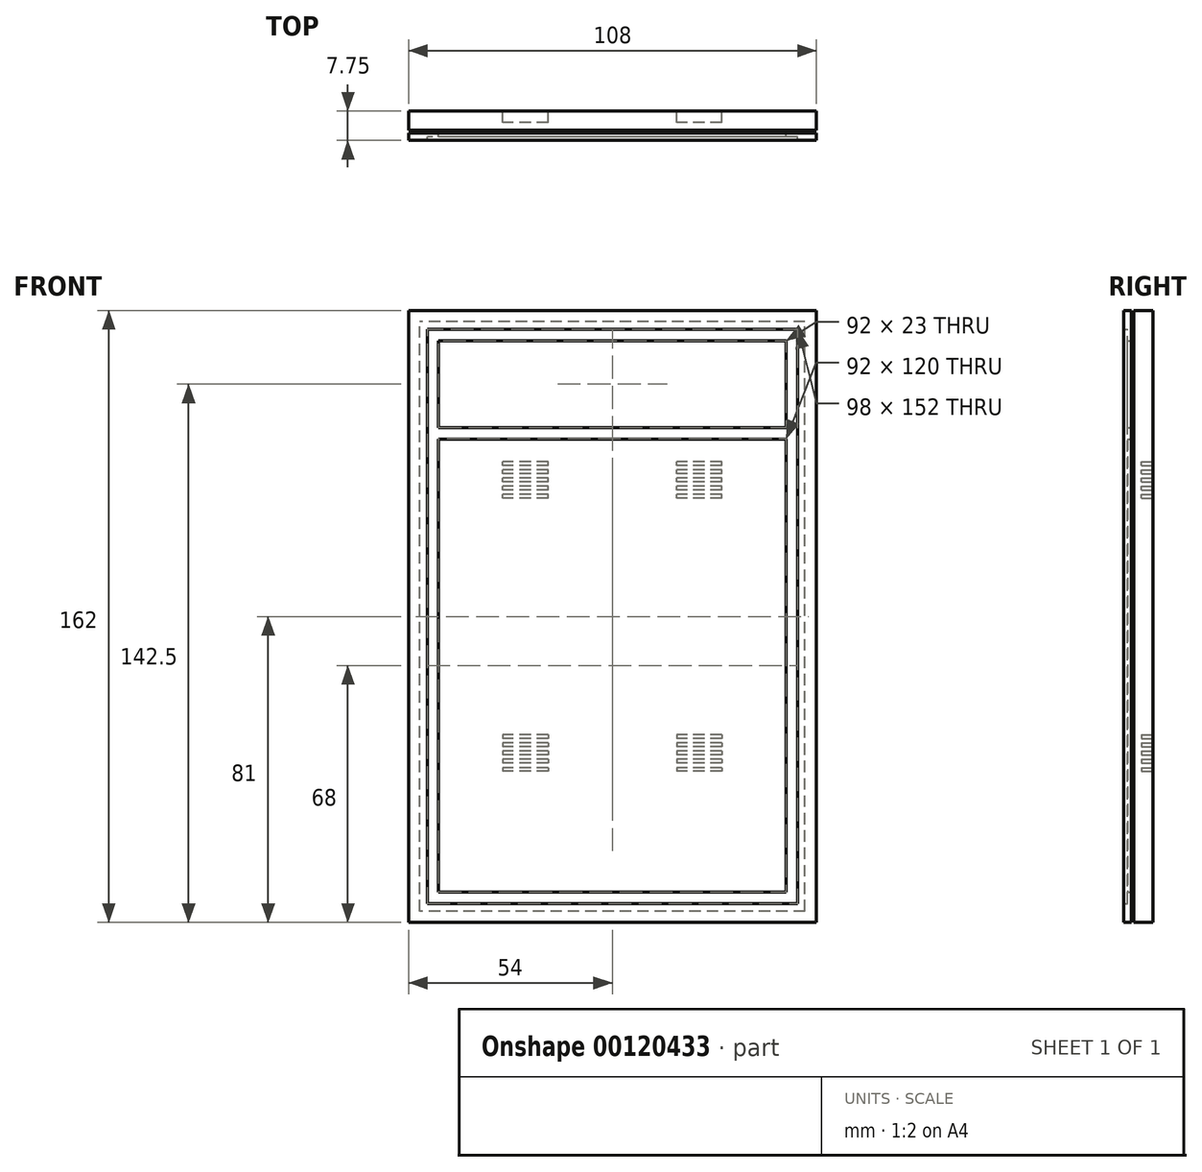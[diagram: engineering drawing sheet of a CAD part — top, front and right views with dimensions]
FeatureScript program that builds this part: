
annotation { "Feature Type Name" : "Feature", "Feature Type Description" : "" }
export const myFeature = defineFeature(function(context is Context, id is Id, definition is map)
    precondition{}
    {
        {
            var Q0;
            Q0=qCreatedBy(makeId("Front.planeOp"),FACE);
            var sketch = newSketch(context, id + "F0", { "sketchPlane" : qUnion([Q0])});
            skLineSegment(sketch, "E0.bottom", {"start": v(54, -81) * mm, "end": v(-54, -81) * mm});
            skLineSegment(sketch, "E0.top", {"start": v(54, 81) * mm, "end": v(-54, 81) * mm});
            skLineSegment(sketch, "E0.left", {"start": v(54, -81) * mm, "end": v(54, 81) * mm});
            skLineSegment(sketch, "E0.right", {"start": v(-54, -81) * mm, "end": v(-54, 81) * mm});
            skPoint(sketch, "E0.middle", {"position": v(0, 0) * mm});
            skLineSegment(sketch, "E1.0", {"start": v(49, 76) * mm, "end": v(-49, 76) * mm});
            skLineSegment(sketch, "E1.1", {"start": v(49, -76) * mm, "end": v(49, 76) * mm});
            skLineSegment(sketch, "E1.2", {"start": v(49, -76) * mm, "end": v(-49, -76) * mm});
            skLineSegment(sketch, "E1.3", {"start": v(-49, -76) * mm, "end": v(-49, 76) * mm});
            skLineSegment(sketch, "E2.bottom", {"start": v(46, -73) * mm, "end": v(-46, -73) * mm});
            skLineSegment(sketch, "E2.top", {"start": v(46, 50) * mm, "end": v(-46, 50) * mm});
            skLineSegment(sketch, "E2.right", {"start": v(-46, -73) * mm, "end": v(-46, 47) * mm});
            skPoint(sketch, "E2.middle", {"position": v(0, -11.5) * mm});
            skLineSegment(sketch, "E3.top", {"start": v(-46, 73) * mm, "end": v(46, 73) * mm});
            skLineSegment(sketch, "E3.left", {"start": v(-46, 50) * mm, "end": v(-46, 73) * mm});
            skLineSegment(sketch, "E3.right", {"start": v(46, 50) * mm, "end": v(46, 73) * mm});
            skLineSegment(sketch, "E4", {"start": v(-46, 47) * mm, "end": v(46, 47) * mm});
            skLineSegment(sketch, "E5", {"start": v(46, 47) * mm, "end": v(46, -73) * mm});
            skLineSegment(sketch, "E6.0", {"start": v(51, 78) * mm, "end": v(-51, 78) * mm});
            skLineSegment(sketch, "E6.1", {"start": v(51, -78) * mm, "end": v(51, 78) * mm});
            skLineSegment(sketch, "E6.2", {"start": v(51, -78) * mm, "end": v(-51, -78) * mm});
            skLineSegment(sketch, "E6.3", {"start": v(-51, -78) * mm, "end": v(-51, 78) * mm});
            skSolve(sketch);
        }
        {
            var Q0;
            Q0=makeQuery(id+"F0.imprint","IMPRINT",FACE,{"disambiguationData":[TD([[makeQuery(id+"F0.imprint","IMPRINT",EDGE,{"derivedFrom":sQuery(id+"F0.wireOp",EDGE,"E0.bottom")}),-1.0]])]});
            var Q1;
            Q1=makeQuery(id+"F0.imprint","IMPRINT",FACE,{"disambiguationData":[TD([[makeQuery(id+"F0.imprint","IMPRINT",EDGE,{"derivedFrom":sQuery(id+"F0.wireOp",EDGE,"E1.0")}),-1.0]])]});
            extrude(context, id + "F1", {"entities" : qUnion([Q0, Q1]), "depth" : 2 * mm});
        }
        {
            var Q0;
            Q0=makeQuery(id+"F0.imprint","IMPRINT",FACE,{"disambiguationData":[TD([[makeQuery(id+"F0.imprint","IMPRINT",EDGE,{"derivedFrom":sQuery(id+"F0.wireOp",EDGE,"E1.0")}),1.0]])]});
            extrude(context, id + "F2", {"entities" : qUnion([Q0]), "depth" : 1 * mm});
        }
        {
            var Q0;
            Q0=makeQuery(id+"F0.imprint","IMPRINT",FACE,{"disambiguationData":[TD([[makeQuery(id+"F0.imprint","IMPRINT",EDGE,{"derivedFrom":sQuery(id+"F0.wireOp",EDGE,"E2.bottom")}),-1.0]])]});
            extrude(context, id + "F3", {"entities" : qUnion([Q0]), "depth" : 1 * mm});
        }
        {
            var Q0;
            Q0=makeQuery(id+"F0.imprint","IMPRINT",FACE,{"disambiguationData":[TD([[makeQuery(id+"F0.imprint","IMPRINT",EDGE,{"derivedFrom":sQuery(id+"F0.wireOp",EDGE,"E2.top")}),-1.0]])]});
            extrude(context, id + "F4", {"entities" : qUnion([Q0]), "depth" : 1 * mm});
        }
        {
            var Q0;
            Q0=makeQuery(id+"F0.imprint","IMPRINT",FACE,{"disambiguationData":[TD([[makeQuery(id+"F0.imprint","IMPRINT",EDGE,{"derivedFrom":sQuery(id+"F0.wireOp",EDGE,"E1.0")}),-1.0]])]});
            extrude(context, id + "F5", {"entities" : qUnion([Q0]), "operationType" : NewBodyOperationType.ADD, "oppositeDirection" : true, "depth" : 0.75 * mm});
        }
        {
            var Q0;
            Q0=makeQuery(id+"F0.imprint","IMPRINT",FACE,{"disambiguationData":[TD([[makeQuery(id+"F0.imprint","IMPRINT",EDGE,{"derivedFrom":sQuery(id+"F0.wireOp",EDGE,"E0.bottom")}),-1.0]])]});
            var Q1;
            Q1=makeQuery(id+"F0.imprint","IMPRINT",FACE,{"disambiguationData":[TD([[makeQuery(id+"F0.imprint","IMPRINT",EDGE,{"derivedFrom":sQuery(id+"F0.wireOp",EDGE,"E1.0")}),-1.0]])]});
            var Q2;
            Q2=makeQuery(id+"F0.imprint","IMPRINT",FACE,{"disambiguationData":[TD([[makeQuery(id+"F0.imprint","IMPRINT",EDGE,{"derivedFrom":sQuery(id+"F0.wireOp",EDGE,"E1.0")}),1.0]])]});
            var Q3;
            Q3=makeQuery(id+"F0.imprint","IMPRINT",FACE,{"disambiguationData":[TD([[makeQuery(id+"F0.imprint","IMPRINT",EDGE,{"derivedFrom":sQuery(id+"F0.wireOp",EDGE,"E2.top")}),-1.0]])]});
            var Q4;
            Q4=makeQuery(id+"F0.imprint","IMPRINT",FACE,{"disambiguationData":[TD([[makeQuery(id+"F0.imprint","IMPRINT",EDGE,{"derivedFrom":sQuery(id+"F0.wireOp",EDGE,"E2.bottom")}),-1.0]])]});
            extrude(context, id + "F6", {"entities" : qUnion([Q0, Q1, Q2, Q3, Q4]), "oppositeDirection" : true, "depth" : 5 * mm});
        }
        {
            var Q0;
            Q0=makeQuery(id+"F6.opExtrude","SWEPT_BODY",BODY,{"disambiguationData":[OSD([sQuery(id+"F0.wireOp",EDGE,"E0.bottom"),sQuery(id+"F0.wireOp",EDGE,"E0.top"),sQuery(id+"F0.wireOp",EDGE,"E0.left"),sQuery(id+"F0.wireOp",EDGE,"E0.right")])]});
            transform(context, id + "F7", {"entities" : qUnion([Q0]), "transformType" : TransformType.TRANSLATION_3D, "dx" : 0 * mm, "dy" : 0.75 * mm, "dz" : 0 * mm, "makeCopy" : false});
        }
        {
            var Q0;
            Q0=makeQuery(id+"F6.opExtrude","CAP_FACE",FACE,{"disambiguationData":[OSD([sQuery(id+"F0.wireOp",EDGE,"E0.bottom"),sQuery(id+"F0.wireOp",EDGE,"E0.top"),sQuery(id+"F0.wireOp",EDGE,"E0.left"),sQuery(id+"F0.wireOp",EDGE,"E0.right")])],"isStart":false});
            var sketch = newSketch(context, id + "F8", { "sketchPlane" : qUnion([Q0])});
            skLineSegment(sketch, "E7.bottom", {"start": v(-29, -40) * mm, "end": v(-17, -40) * mm});
            skLineSegment(sketch, "E7.top", {"start": v(-29, -41) * mm, "end": v(-17, -41) * mm});
            skLineSegment(sketch, "E7.left", {"start": v(-29, -40) * mm, "end": v(-29, -41) * mm});
            skLineSegment(sketch, "E7.right", {"start": v(-17, -40) * mm, "end": v(-17, -41) * mm});
            skLineSegment(sketch, "E8.0.1.0", {"start": v(-29, -37.82) * mm, "end": v(-17, -37.82) * mm});
            skLineSegment(sketch, "E8.0.1.1", {"start": v(-29, -38.82) * mm, "end": v(-17, -38.82) * mm});
            skLineSegment(sketch, "E8.0.1.2", {"start": v(-17, -37.82) * mm, "end": v(-17, -38.82) * mm});
            skLineSegment(sketch, "E8.0.1.3", {"start": v(-29, -37.82) * mm, "end": v(-29, -38.82) * mm});
            skLineSegment(sketch, "E8.0.2.0", {"start": v(-29, -35.64) * mm, "end": v(-17, -35.64) * mm});
            skLineSegment(sketch, "E8.0.2.1", {"start": v(-29, -36.64) * mm, "end": v(-17, -36.64) * mm});
            skLineSegment(sketch, "E8.0.2.2", {"start": v(-17, -35.64) * mm, "end": v(-17, -36.64) * mm});
            skLineSegment(sketch, "E8.0.2.3", {"start": v(-29, -35.64) * mm, "end": v(-29, -36.64) * mm});
            skLineSegment(sketch, "E8.0.3.0", {"start": v(-29, -33.45) * mm, "end": v(-17, -33.45) * mm});
            skLineSegment(sketch, "E8.0.3.1", {"start": v(-29, -34.45) * mm, "end": v(-17, -34.45) * mm});
            skLineSegment(sketch, "E8.0.3.2", {"start": v(-17, -33.45) * mm, "end": v(-17, -34.45) * mm});
            skLineSegment(sketch, "E8.0.3.3", {"start": v(-29, -33.45) * mm, "end": v(-29, -34.45) * mm});
            skLineSegment(sketch, "E8.0.4.0", {"start": v(-29, -31.27) * mm, "end": v(-17, -31.27) * mm});
            skLineSegment(sketch, "E8.0.4.1", {"start": v(-29, -32.27) * mm, "end": v(-17, -32.27) * mm});
            skLineSegment(sketch, "E8.0.4.2", {"start": v(-17, -31.27) * mm, "end": v(-17, -32.27) * mm});
            skLineSegment(sketch, "E8.0.4.3", {"start": v(-29, -31.27) * mm, "end": v(-29, -32.27) * mm});
            skLineSegment(sketch, "E8.1.0.0", {"start": v(17, -40) * mm, "end": v(29, -40) * mm});
            skLineSegment(sketch, "E8.1.0.1", {"start": v(17, -41) * mm, "end": v(29, -41) * mm});
            skLineSegment(sketch, "E8.1.0.2", {"start": v(29, -40) * mm, "end": v(29, -41) * mm});
            skLineSegment(sketch, "E8.1.0.3", {"start": v(17, -40) * mm, "end": v(17, -41) * mm});
            skLineSegment(sketch, "E8.1.1.0", {"start": v(17, -37.82) * mm, "end": v(29, -37.82) * mm});
            skLineSegment(sketch, "E8.1.1.1", {"start": v(17, -38.82) * mm, "end": v(29, -38.82) * mm});
            skLineSegment(sketch, "E8.1.1.2", {"start": v(29, -37.82) * mm, "end": v(29, -38.82) * mm});
            skLineSegment(sketch, "E8.1.1.3", {"start": v(17, -37.82) * mm, "end": v(17, -38.82) * mm});
            skLineSegment(sketch, "E8.1.2.0", {"start": v(17, -35.64) * mm, "end": v(29, -35.64) * mm});
            skLineSegment(sketch, "E8.1.2.1", {"start": v(17, -36.64) * mm, "end": v(29, -36.64) * mm});
            skLineSegment(sketch, "E8.1.2.2", {"start": v(29, -35.64) * mm, "end": v(29, -36.64) * mm});
            skLineSegment(sketch, "E8.1.2.3", {"start": v(17, -35.64) * mm, "end": v(17, -36.64) * mm});
            skLineSegment(sketch, "E8.1.3.0", {"start": v(17, -33.45) * mm, "end": v(29, -33.45) * mm});
            skLineSegment(sketch, "E8.1.3.1", {"start": v(17, -34.45) * mm, "end": v(29, -34.45) * mm});
            skLineSegment(sketch, "E8.1.3.2", {"start": v(29, -33.45) * mm, "end": v(29, -34.45) * mm});
            skLineSegment(sketch, "E8.1.3.3", {"start": v(17, -33.45) * mm, "end": v(17, -34.45) * mm});
            skLineSegment(sketch, "E8.1.4.0", {"start": v(17, -31.27) * mm, "end": v(29, -31.27) * mm});
            skLineSegment(sketch, "E8.1.4.1", {"start": v(17, -32.27) * mm, "end": v(29, -32.27) * mm});
            skLineSegment(sketch, "E8.1.4.2", {"start": v(29, -31.27) * mm, "end": v(29, -32.27) * mm});
            skLineSegment(sketch, "E8.1.4.3", {"start": v(17, -31.27) * mm, "end": v(17, -32.27) * mm});
            skLineSegment(sketch, "E8.direction1", {"start": v(-29, -40) * mm, "end": v(17, -40) * mm, "construction": true});
            skLineSegment(sketch, "E8.direction2", {"start": v(-29, -40) * mm, "end": v(-29, -37.82) * mm, "construction": true});
            skLineSegment(sketch, "E9.MirrorCS", {"start": v(-29, 40) * mm, "end": v(-29, 37.82) * mm, "construction": true});
            skLineSegment(sketch, "E10.MirrorCS", {"start": v(-17, 33.45) * mm, "end": v(-17, 34.45) * mm});
            skLineSegment(sketch, "E11.MirrorCS", {"start": v(-29, 33.45) * mm, "end": v(-29, 34.45) * mm});
            skLineSegment(sketch, "E12.MirrorCS", {"start": v(-29, 40) * mm, "end": v(-29, 41) * mm});
            skLineSegment(sketch, "E13.MirrorCS", {"start": v(-29, 37.82) * mm, "end": v(-29, 38.82) * mm});
            skLineSegment(sketch, "E14.MirrorCS", {"start": v(-17, 40) * mm, "end": v(-17, 41) * mm});
            skLineSegment(sketch, "E15.MirrorCS", {"start": v(-29, 31.27) * mm, "end": v(-29, 32.27) * mm});
            skLineSegment(sketch, "E16.MirrorCS", {"start": v(-29, 35.64) * mm, "end": v(-29, 36.64) * mm});
            skLineSegment(sketch, "E17.MirrorCS", {"start": v(-17, 35.64) * mm, "end": v(-17, 36.64) * mm});
            skLineSegment(sketch, "E18.MirrorCS", {"start": v(-17, 37.82) * mm, "end": v(-17, 38.82) * mm});
            skLineSegment(sketch, "E19.MirrorCS", {"start": v(-17, 31.27) * mm, "end": v(-17, 32.27) * mm});
            skLineSegment(sketch, "E20.MirrorCS", {"start": v(-29, 32.27) * mm, "end": v(-17, 32.27) * mm});
            skLineSegment(sketch, "E21.MirrorCS", {"start": v(-29, 34.45) * mm, "end": v(-17, 34.45) * mm});
            skLineSegment(sketch, "E22.MirrorCS", {"start": v(-29, 40) * mm, "end": v(-17, 40) * mm});
            skLineSegment(sketch, "E23.MirrorCS", {"start": v(-29, 41) * mm, "end": v(-17, 41) * mm});
            skLineSegment(sketch, "E24.MirrorCS", {"start": v(-29, 37.82) * mm, "end": v(-17, 37.82) * mm});
            skLineSegment(sketch, "E25.MirrorCS", {"start": v(-29, 33.45) * mm, "end": v(-17, 33.45) * mm});
            skLineSegment(sketch, "E26.MirrorCS", {"start": v(-29, 36.64) * mm, "end": v(-17, 36.64) * mm});
            skLineSegment(sketch, "E27.MirrorCS", {"start": v(-29, 35.64) * mm, "end": v(-17, 35.64) * mm});
            skLineSegment(sketch, "E28.MirrorCS", {"start": v(-29, 31.27) * mm, "end": v(-17, 31.27) * mm});
            skLineSegment(sketch, "E29.MirrorCS", {"start": v(-29, 38.82) * mm, "end": v(-17, 38.82) * mm});
            skLineSegment(sketch, "E30.MirrorCS", {"start": v(17, 40) * mm, "end": v(17, 41) * mm});
            skLineSegment(sketch, "E31.MirrorCS", {"start": v(17, 35.64) * mm, "end": v(17, 36.64) * mm});
            skLineSegment(sketch, "E32.MirrorCS", {"start": v(29, 33.45) * mm, "end": v(29, 34.45) * mm});
            skLineSegment(sketch, "E33.MirrorCS", {"start": v(17, 37.82) * mm, "end": v(17, 38.82) * mm});
            skLineSegment(sketch, "E34.MirrorCS", {"start": v(29, 40) * mm, "end": v(29, 41) * mm});
            skLineSegment(sketch, "E35.MirrorCS", {"start": v(29, 31.27) * mm, "end": v(29, 32.27) * mm});
            skLineSegment(sketch, "E36.MirrorCS", {"start": v(29, 37.82) * mm, "end": v(29, 38.82) * mm});
            skLineSegment(sketch, "E37.MirrorCS", {"start": v(29, 35.64) * mm, "end": v(29, 36.64) * mm});
            skLineSegment(sketch, "E38.MirrorCS", {"start": v(17, 33.45) * mm, "end": v(17, 34.45) * mm});
            skLineSegment(sketch, "E39.MirrorCS", {"start": v(17, 31.27) * mm, "end": v(17, 32.27) * mm});
            skLineSegment(sketch, "E40.MirrorCS", {"start": v(17, 40) * mm, "end": v(29, 40) * mm});
            skLineSegment(sketch, "E41.MirrorCS", {"start": v(17, 36.64) * mm, "end": v(29, 36.64) * mm});
            skLineSegment(sketch, "E42.MirrorCS", {"start": v(17, 31.27) * mm, "end": v(29, 31.27) * mm});
            skLineSegment(sketch, "E43.MirrorCS", {"start": v(17, 38.82) * mm, "end": v(29, 38.82) * mm});
            skLineSegment(sketch, "E44.MirrorCS", {"start": v(17, 37.82) * mm, "end": v(29, 37.82) * mm});
            skLineSegment(sketch, "E45.MirrorCS", {"start": v(17, 33.45) * mm, "end": v(29, 33.45) * mm});
            skLineSegment(sketch, "E46.MirrorCS", {"start": v(17, 41) * mm, "end": v(29, 41) * mm});
            skLineSegment(sketch, "E47.MirrorCS", {"start": v(17, 32.27) * mm, "end": v(29, 32.27) * mm});
            skLineSegment(sketch, "E48.MirrorCS", {"start": v(17, 35.64) * mm, "end": v(29, 35.64) * mm});
            skLineSegment(sketch, "E49.MirrorCS", {"start": v(17, 34.45) * mm, "end": v(29, 34.45) * mm});
            skSolve(sketch);
        }
        {
            var Q0;
            Q0 = qSketchRegion(id + "F8", true);
            extrude(context, id + "F9", {"entities" : qUnion([Q0]), "operationType" : NewBodyOperationType.REMOVE, "oppositeDirection" : true, "depth" : 3 * mm});
        }
    });
